# Revit family: Casement_41_C_Top_Hung_HD_Custom
name_source: partatom
category: Windows
revit_build: Autodesk Revit 2014 (Build: 20130308_1515(x64)
units: mm (PartAtom-declared; Revit-internal decimal feet)

## types (1)
- 41-TypeC-T-HD-Custom
    Corrected Mullion Configuration = 2 mm  [stored 0.00656168 ft]
    Description = Window 41mm, Type C, Top hung, Heavy duty sash, Custom
    Frame Profile Thickness = 41 mm  [stored 0.134514 ft]
    Heavy Duty Sash = Yes
    Limit Fixed Pane Height Max = 3000 mm  [stored 9.84252 ft]
    Limit Fixed Pane Height Min = 200 mm  [stored 0.656168 ft]
    Limit Fixed Pane Width Max = 3000 mm  [stored 9.84252 ft]
    Limit Fixed Pane Width Min = 200 mm  [stored 0.656168 ft]
    Limit Sash Height Max = 1200 mm  [stored 3.93701 ft]
    Limit Sash Height Min = 300 mm  [stored 0.984252 ft]
    Limit Sash Width Max = 1500 mm  [stored 4.92126 ft]
    Limit Sash Width Min = 300 mm  [stored 0.984252 ft]
    Limit Window Height Max = 1288 mm
    Limit Window Height Min = 388 mm
    Manufacturer = Crealco
    Max System DG Unit Thickness = 25 mm  [stored 0.082021 ft]
    Model = Casement 41
    Rough Width = 3 mm  [stored 0.00984252 ft]
    Sash Side Gap = 44 mm
    Standard Mullion Different = No
    Standard Sash = No
    URL = http://www.crealco.co.za
    Wall Closure = By host

note: [stored X ft] marks values corroborated as IEEE doubles in the binary element streams (Revit-internal decimal feet)

## geometry (parser evidence)
native form markers: Sweep x26
no freeform markers — native parametric forms only
